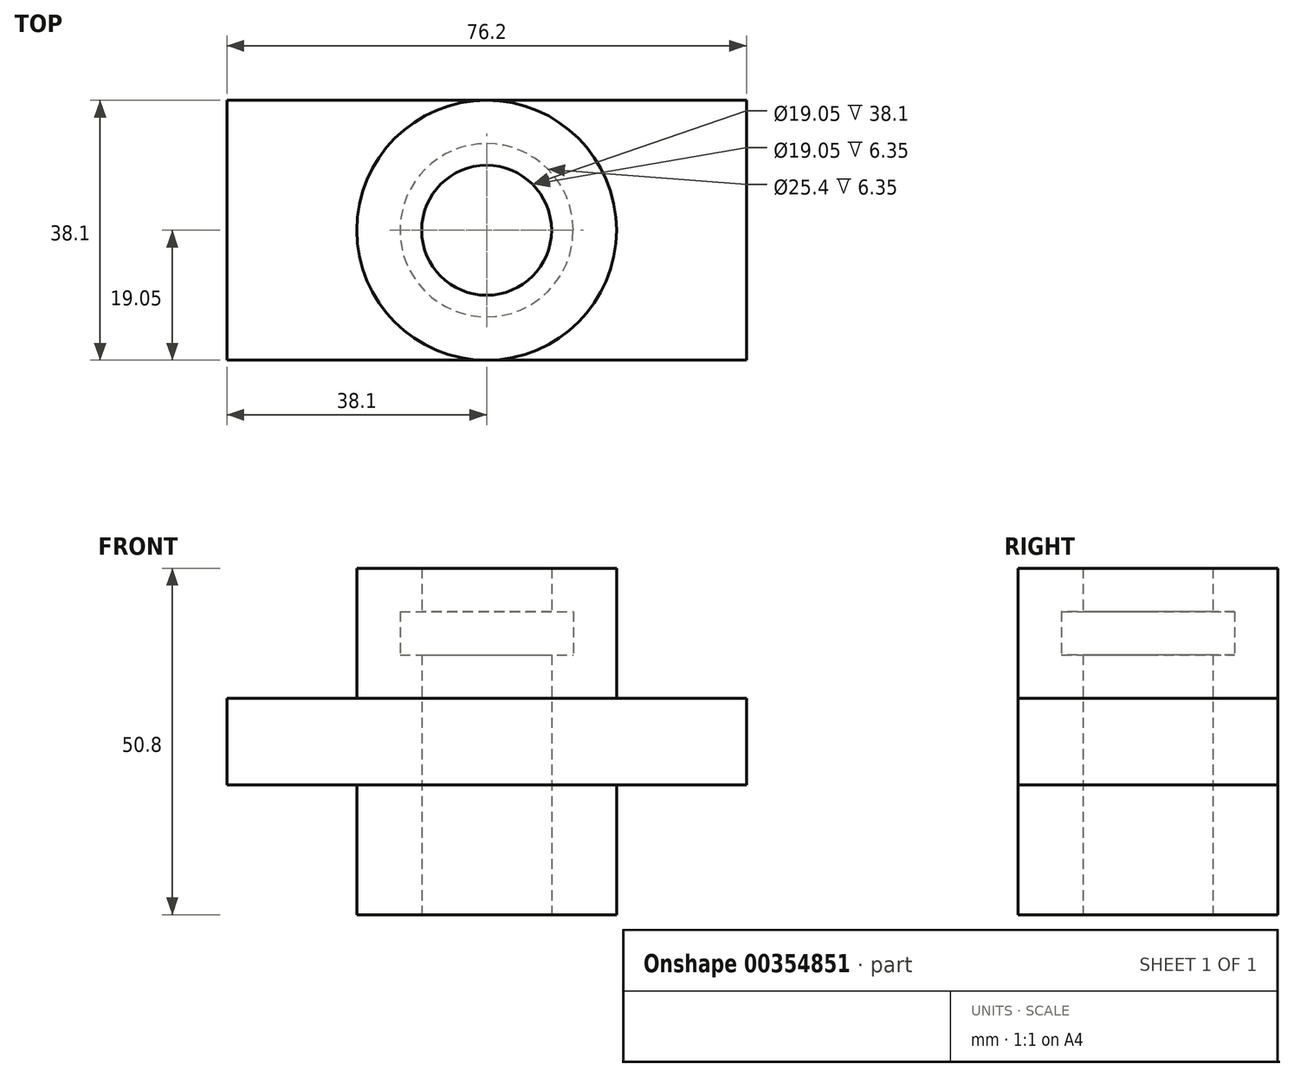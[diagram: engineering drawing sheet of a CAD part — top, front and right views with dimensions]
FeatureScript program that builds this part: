
annotation { "Feature Type Name" : "Feature", "Feature Type Description" : "" }
export const myFeature = defineFeature(function(context is Context, id is Id, definition is map)
    precondition{}
    {
        {
            var Q0;
            Q0=qCreatedBy(makeId("Top.planeOp"),FACE);
            var sketch = newSketch(context, id + "F0", { "sketchPlane" : qUnion([Q0])});
            skCircle(sketch, "E0", {"center": v(0, 0) * mm, "radius": 19.05 * mm});
            skCircle(sketch, "E1", {"center": v(0, 0) * mm, "radius": 9.53 * mm});
            skSolve(sketch);
        }
        {
            var Q0;
            Q0 = qSketchRegion(id + "F0", true);
            extrude(context, id + "F1", {"entities" : qUnion([Q0]), "depth" : 50.8 * mm, "symmetric" : true});
        }
        {
            var Q0;
            Q0=qCreatedBy(makeId("Top.planeOp"),FACE);
            var sketch = newSketch(context, id + "F2", { "sketchPlane" : qUnion([Q0])});
            skLineSegment(sketch, "E2.bottom", {"start": v(-38.1, 19.05) * mm, "end": v(38.1, 19.05) * mm});
            skLineSegment(sketch, "E2.top", {"start": v(-38.1, -19.05) * mm, "end": v(38.1, -19.05) * mm});
            skLineSegment(sketch, "E2.left", {"start": v(-38.1, 19.05) * mm, "end": v(-38.1, -19.05) * mm});
            skLineSegment(sketch, "E2.right", {"start": v(38.1, 19.05) * mm, "end": v(38.1, -19.05) * mm});
            skLineSegment(sketch, "E3", {"start": v(0, 47.87) * mm, "end": v(0, -44.05) * mm, "construction": true});
            skCircle(sketch, "E4", {"center": v(0, 0) * mm, "radius": 9.53 * mm});
            skSolve(sketch);
        }
        {
            var Q0;
            Q0 = qSketchRegion(id + "F2", true);
            extrude(context, id + "F3", {"entities" : qUnion([Q0]), "operationType" : NewBodyOperationType.ADD, "depth" : 12.7 * mm, "symmetric" : true});
        }
        {
            var Q0;
            Q0=makeQuery(id+"F2.imprint","IMPRINT",FACE,{"disambiguationData":[TD([[makeQuery(id+"F2.imprint","IMPRINT",EDGE,{"derivedFrom":sQuery(id+"F2.wireOp",EDGE,"E4")}),1.0]])]});
            extrude(context, id + "F4", {"entities" : qUnion([Q0]), "operationType" : NewBodyOperationType.REMOVE, "endBound" : BoundingType.THROUGH_ALL, "oppositeDirection" : true, "depth" : 25.4 * mm});
        }
        {
            var Q0;
            Q0=qCreatedBy(makeId("Front.planeOp"),FACE);
            var sketch = newSketch(context, id + "F5", { "sketchPlane" : qUnion([Q0])});
            skLineSegment(sketch, "E5", {"start": v(0, 46.56) * mm, "end": v(0, -44.6) * mm, "construction": true});
            skLineSegment(sketch, "E6.left", {"start": v(-12.7, 19.05) * mm, "end": v(-12.7, 12.7) * mm});
            skLineSegment(sketch, "E7", {"start": v(0, 19.05) * mm, "end": v(0, 12.7) * mm});
            skLineSegment(sketch, "E8", {"start": v(0, 12.7) * mm, "end": v(-12.7, 12.7) * mm});
            skLineSegment(sketch, "E9", {"start": v(-12.7, 19.05) * mm, "end": v(0, 19.05) * mm});
            skSolve(sketch);
        }
        {
            var Q0;
            Q0 = qSketchRegion(id + "F5", true);
            var Q1;
            Q1=sQuery(id+"F5.wireOp",EDGE,"E5");
            revolve(context, id + "F6", {"operationType" : NewBodyOperationType.REMOVE, "entities" : qUnion([Q0]), "axis" : qUnion([Q1]), "revolveType" : RevolveType.FULL, "oppositeDirection" : true});
        }
    });
